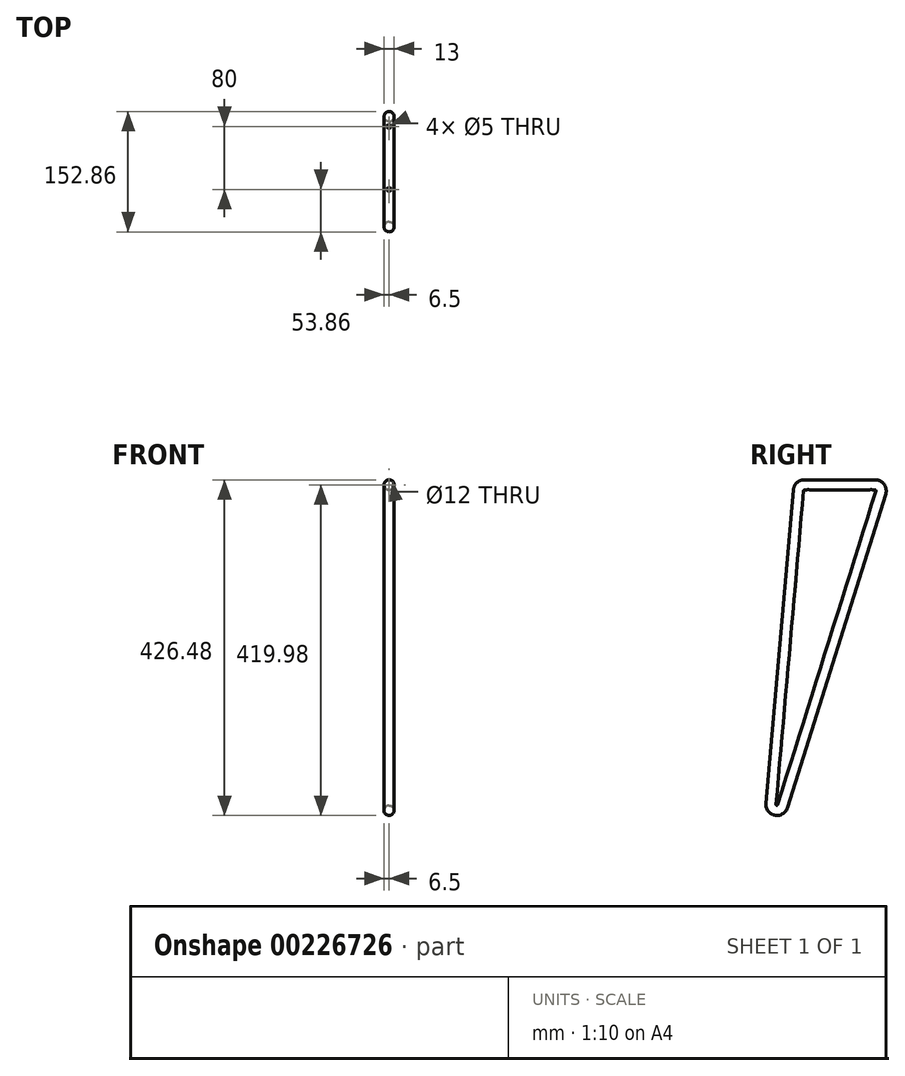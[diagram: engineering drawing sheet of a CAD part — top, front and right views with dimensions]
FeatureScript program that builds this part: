
annotation { "Feature Type Name" : "Feature", "Feature Type Description" : "" }
export const myFeature = defineFeature(function(context is Context, id is Id, definition is map)
    precondition{}
    {
        {
            var Q0;
            Q0=qCreatedBy(makeId("Right.planeOp"),FACE);
            var sketch = newSketch(context, id + "F0", { "sketchPlane" : qUnion([Q0])});
            skArc(sketch, "E0", {"start": v(0, 7.5) * mm, "mid": v(-5.07, 5.53) * mm, "end": v(-7.47, 0.65) * mm});
            skArc(sketch, "E1", {"start": v(97.16, -2.24) * mm, "mid": v(96.04, 4.44) * mm, "end": v(90, 7.5) * mm});
            skArc(sketch, "E2", {"start": v(-42.33, -397.82) * mm, "mid": v(-36.32, -405.84) * mm, "end": v(-27.7, -400.72) * mm});
            skLineSegment(sketch, "E3", {"start": v(0, 7.5) * mm, "end": v(90, 7.5) * mm});
            skLineSegment(sketch, "E4", {"start": v(97.16, -2.24) * mm, "end": v(-27.7, -400.72) * mm});
            skLineSegment(sketch, "E5", {"start": v(-7.47, 0.65) * mm, "end": v(-42.33, -397.82) * mm});
            skSolve(sketch);
        }
        {
            var Q0;
            Q0=qCreatedBy(makeId("Front.planeOp"),FACE);
            var sketch = newSketch(context, id + "F1", { "sketchPlane" : qUnion([Q0])});
            skCircle(sketch, "E6", {"center": v(0, 7.5) * mm, "radius": 6.5 * mm});
            skCircle(sketch, "E7", {"center": v(0, 7.5) * mm, "radius": 6 * mm});
            skSolve(sketch);
        }
        {
            var Q0;
            Q0=makeQuery(id+"F1.imprint","IMPRINT",FACE,{"disambiguationData":[TD([[makeQuery(id+"F1.imprint","IMPRINT",EDGE,{"derivedFrom":sQuery(id+"F1.wireOp",EDGE,"E6")}),1.0]])]});
            var Q1;
            Q1=sQuery(id+"F0.wireOp",EDGE,"E3");
            var Q2;
            Q2=sQuery(id+"F0.wireOp",EDGE,"E1");
            var Q3;
            Q3=sQuery(id+"F0.wireOp",EDGE,"E4");
            var Q4;
            Q4=sQuery(id+"F0.wireOp",EDGE,"E2");
            var Q5;
            Q5=sQuery(id+"F0.wireOp",EDGE,"E5");
            var Q6;
            Q6=sQuery(id+"F0.wireOp",EDGE,"E0");
            sweep(context, id + "F2", {"profiles" : qUnion([Q0]), "path" : qUnion([Q1, Q2, Q3, Q4, Q5, Q6])});
        }
        {
            var Q0;
            Q0=qCreatedBy(makeId("Top.planeOp"),FACE);
            var sketch = newSketch(context, id + "F3", { "sketchPlane" : qUnion([Q0])});
            skCircle(sketch, "E8", {"center": v(0, 5) * mm, "radius": 2.5 * mm});
            skCircle(sketch, "E9", {"center": v(0, 85) * mm, "radius": 2.5 * mm});
            skSolve(sketch);
        }
        {
            var Q0;
            Q0 = qSketchRegion(id + "F3", true);
            extrude(context, id + "F4", {"entities" : qUnion([Q0]), "operationType" : NewBodyOperationType.REMOVE, "endBound" : BoundingType.THROUGH_ALL, "depth" : 25 * mm});
        }
    });
